# Revit family: Gira_212000
name_source: partatom
category: Electrical Fixtures
revit_build: Autodesk Revit 2017 (Build: 20160225_1515(x64)
units: mm (PartAtom-declared; Revit-internal decimal feet)

## family parameters
Cut with Voids When Loaded = No
Host = Face
Maintain Annotation Orientation = No
Part Type = Normal
Room Calculation Point = No
Round Connector Dimension = Use Diameter
Shared = No

## types (1)
- Pow.supply 160 mA choke KNX DRA
    BIM = https://media.live.bim.site 8f.rfa
    BIMSITE_PRODUCT_ID = f22732c19fceb7285109560b0cfdd15072a671c7
    Bus connection included = No
    Cost = 0 $
    Default Elevation = 1219 mm
    Description = PS 160mA choke DRA KNX KNX power supply 160 mA with integrated choke, Power supplies for supplying KNX devices with bus voltage.,Features: - Output with integrated choke to supply KNX bus lines. - Output DC 30 V to supply additional devices. - Rated current can be flexibly split up amongst outputs. - Reset button. - Short-circuit-proof. - Overvoltage protection. - Open circuit-proof. - Suitable for operation in systems with emergency power supply. - Isolated signal contact for operating message and diagnostic message. - Two KNX power supplies of the same type can be connected in parallel.,Notes : - Installation on DIN top-hat rail. - VDE approval in accordance with EN 60669-1, EN 60669-2-1.
    GTIN = 4010337023210
    HAN = 212000
    Handschaltung = No
    HeinzeBIM = https://www.heinze.de
    Local operation/hand operation = No
    Manufacturer = Gira
    Max. number of venetian-blind outputs = 0
    Number of binary inputs = 0
    Number of inputs = 0
    Number of outputs = 0
    Rated current [Ampere] = 0
    Stellgröße schaltend = No
    Stellgröße stetig = No
    Suitable for C-load = No
    URL = https://www.gira.de
    Ventilschutzfunktion = No
    With switch function = No

## geometry (parser evidence)
native form markers: Blend x2, Sweep x3
no freeform markers — native parametric forms only
